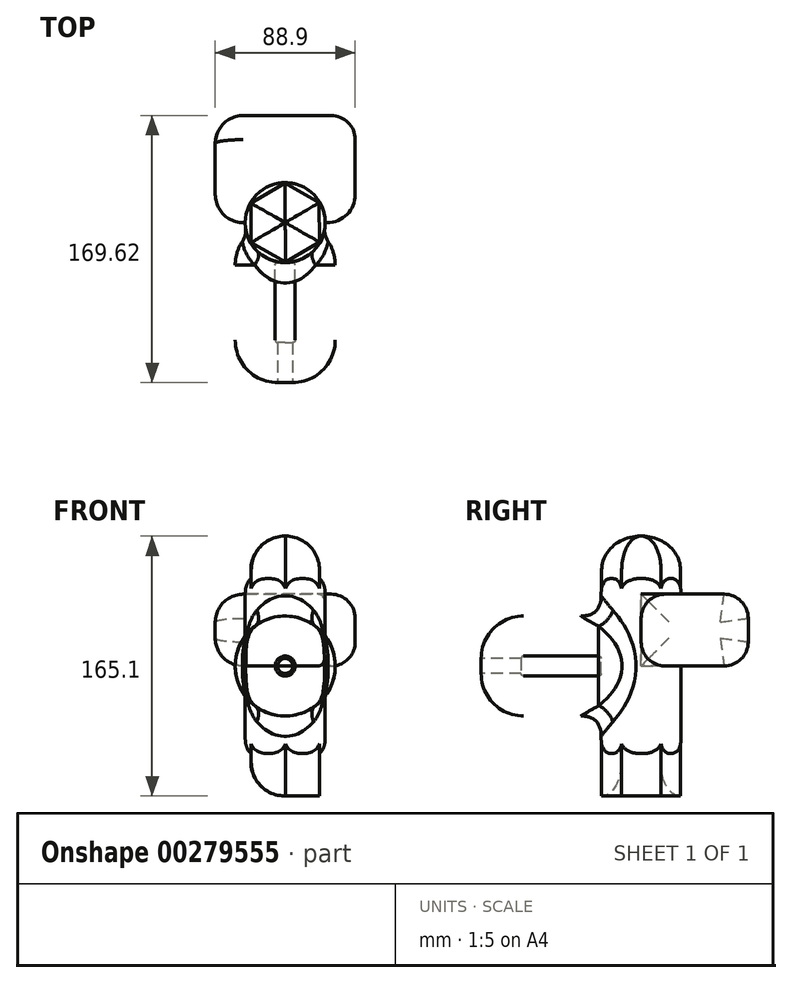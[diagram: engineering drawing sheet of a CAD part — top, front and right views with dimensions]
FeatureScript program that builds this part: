
annotation { "Feature Type Name" : "Feature", "Feature Type Description" : "" }
export const myFeature = defineFeature(function(context is Context, id is Id, definition is map)
    precondition{}
    {
        {
            var Q0;
            Q0=qCreatedBy(makeId("Front.planeOp"),FACE);
            var sketch = newSketch(context, id + "F0", { "sketchPlane" : qUnion([Q0])});
            skCircle(sketch, "E0", {"center": v(0, 0) * mm, "radius": 31.75 * mm});
            skSolve(sketch);
        }
        {
            var Q0;
            Q0=makeQuery(id+"F0.imprint","IMPRINT",FACE,{"disambiguationData":[TD([[makeQuery(id+"F0.imprint","IMPRINT",EDGE,{"derivedFrom":sQuery(id+"F0.wireOp",EDGE,"E0")}),1.0]])]});
            extrude(context, id + "F1", {"entities" : qUnion([Q0]), "depth" : 101.6 * mm});
        }
        {
            var Q0;
            Q0=makeQuery(id+"F1.opExtrude","CAP_FACE",FACE,{"disambiguationData":[OSD([sQuery(id+"F0.wireOp",EDGE,"E0")])],"isStart":false});
            var Q1;
            Q1=makeQuery(id+"F1.opExtrude","CAP_EDGE",EDGE,{"disambiguationData":[OSD([sQuery(id+"F0.wireOp",EDGE,"E0")])],"isStart":true});
            fillet(context, id + "F2", {"entities" : qUnion([Q0, Q1]), "radius" : 26.98 * mm, "tangentPropagation" : true, "allowEdgeOverflow" : false});
        }
        {
            var Q0;
            Q0=makeQuery(id+"F1.opExtrude","CAP_FACE",FACE,{"disambiguationData":[OSD([sQuery(id+"F0.wireOp",EDGE,"E0")])],"isStart":false});
            shell(context, id + "F3", {"entities" : qUnion([Q0]), "thickness" : 25.4 * mm});
        }
        {
            var Q0;
            Q0=qCreatedBy(makeId("Top.planeOp"),FACE);
            var sketch = newSketch(context, id + "F4", { "sketchPlane" : qUnion([Q0])});
            skCircle(sketch, "E1", {"center": v(0, 0) * mm, "radius": 25.4 * mm});
            skSolve(sketch);
        }
        {
            var Q0;
            Q0 = qSketchRegion(id + "F4", true);
            extrude(context, id + "F5", {"entities" : qUnion([Q0]), "operationType" : NewBodyOperationType.ADD, "endBound" : BoundingType.SYMMETRIC, "depth" : 116.84 * mm});
        }
        {
            var Q0;
            Q0=makeQuery(id+"F5.opExtrude","SWEPT_FACE",FACE,{"disambiguationData":[OSD([sQuery(id+"F4.wireOp",EDGE,"E1")])]});
            var Q1;
            Q1=makeQuery(id+"F5.opExtrude","CAP_EDGE",EDGE,{"disambiguationData":[OSD([sQuery(id+"F4.wireOp",EDGE,"E1")])],"isStart":false});
            fillet(context, id + "F6", {"entities" : qUnion([Q0, Q1]), "radius" : 12.88 * mm, "tangentPropagation" : true, "rho" : 0.5, "crossSection" : FilletCrossSection.CONIC, "allowEdgeOverflow" : false});
        }
        {
            var Q0;
            Q0=qCreatedBy(makeId("Right.planeOp"),FACE);
            var sketch = newSketch(context, id + "F7", { "sketchPlane" : qUnion([Q0])});
            skLineSegment(sketch, "E2.bottom", {"start": v(0, 0) * mm, "end": v(68.02, 0) * mm});
            skLineSegment(sketch, "E2.top", {"start": v(0, 45.65) * mm, "end": v(68.02, 45.65) * mm});
            skLineSegment(sketch, "E2.left", {"start": v(0, 0) * mm, "end": v(0, 45.65) * mm});
            skLineSegment(sketch, "E2.right", {"start": v(68.02, 0) * mm, "end": v(68.02, 45.65) * mm});
            skSolve(sketch);
        }
        {
            var Q0;
            Q0=makeQuery(id+"F7.imprint","IMPRINT",FACE,{"disambiguationData":[TD([[makeQuery(id+"F7.imprint","IMPRINT",EDGE,{"derivedFrom":sQuery(id+"F7.wireOp",EDGE,"E2.bottom")}),1.0]])]});
            extrude(context, id + "F8", {"entities" : qUnion([Q0]), "operationType" : NewBodyOperationType.ADD, "endBound" : BoundingType.SYMMETRIC, "depth" : 88.9 * mm});
        }
        {
            var Q0;
            Q0=makeQuery(id+"F8.opExtrude","CAP_FACE",FACE,{"disambiguationData":[OSD([sQuery(id+"F7.wireOp",EDGE,"E2.bottom"),sQuery(id+"F7.wireOp",EDGE,"E2.top"),sQuery(id+"F7.wireOp",EDGE,"E2.left"),sQuery(id+"F7.wireOp",EDGE,"E2.right")])],"isStart":true});
            var Q1;
            Q1=makeQuery(id+"F8.opExtrude","CAP_EDGE",EDGE,{"disambiguationData":[OSD([sQuery(id+"F7.wireOp",EDGE,"E2.left")])],"isStart":false});
            fillet(context, id + "F9", {"entities" : qUnion([Q0, Q1]), "radius" : 17.78 * mm, "tangentPropagation" : true, "allowEdgeOverflow" : false});
        }
        {
            var Q0;
            Q0=makeQuery(id+"F8.opExtrude","CAP_EDGE",EDGE,{"disambiguationData":[OSD([sQuery(id+"F7.wireOp",EDGE,"E2.right")])],"isStart":false});
            var Q1;
            Q1=makeQuery(id+"F9.opFillet","BLEND_FACE",FACE,{"disambiguationData":[OSD([sQuery(id+"F7.wireOp",EDGE,"E2.right")])]});
            var Q2;
            Q2=makeQuery(id+"F8.opExtrude","CAP_FACE",FACE,{"disambiguationData":[OSD([sQuery(id+"F7.wireOp",EDGE,"E2.bottom"),sQuery(id+"F7.wireOp",EDGE,"E2.top"),sQuery(id+"F7.wireOp",EDGE,"E2.left"),sQuery(id+"F7.wireOp",EDGE,"E2.right")])],"isStart":false});
            fillet(context, id + "F10", {"entities" : qUnion([Q0, Q1, Q2]), "radius" : 15.33 * mm, "tangentPropagation" : true, "allowEdgeOverflow" : false});
        }
        {
            var Q0;
            Q0=qCreatedBy(makeId("Top.planeOp"),FACE);
            var sketch = newSketch(context, id + "F11", { "sketchPlane" : qUnion([Q0])});
            skCircle(sketch, "E3.cCircle", {"center": v(0, 0) * mm, "radius": 21.7 * mm, "construction": true});
            skLineSegment(sketch, "E3.0", {"start": v(-0.19, 25.05) * mm, "end": v(21.6, 12.7) * mm});
            skLineSegment(sketch, "E3.1", {"start": v(21.6, 12.7) * mm, "end": v(21.8, -12.36) * mm});
            skLineSegment(sketch, "E3.2", {"start": v(21.8, -12.36) * mm, "end": v(0.19, -25.05) * mm});
            skLineSegment(sketch, "E3.3", {"start": v(0.19, -25.05) * mm, "end": v(-21.6, -12.7) * mm});
            skLineSegment(sketch, "E3.4", {"start": v(-21.6, -12.7) * mm, "end": v(-21.8, 12.36) * mm});
            skLineSegment(sketch, "E3.5", {"start": v(-21.8, 12.36) * mm, "end": v(-0.19, 25.05) * mm});
            skPoint(sketch, "E3.0.midPoint", {"position": v(10.7, 18.87) * mm});
            skSolve(sketch);
        }
        {
            var Q0;
            Q0 = qSketchRegion(id + "F11", true);
            extrude(context, id + "F12", {"entities" : qUnion([Q0]), "operationType" : NewBodyOperationType.ADD, "endBound" : BoundingType.SYMMETRIC, "depth" : 165.1 * mm});
        }
        {
            var Q0;
            Q0=makeQuery(id+"F12.opExtrude","CAP_EDGE",EDGE,{"disambiguationData":[OSD([sQuery(id+"F11.wireOp",EDGE,"E3.4")])],"isStart":true});
            var Q1;
            Q1=makeQuery(id+"F12.opExtrude","CAP_FACE",FACE,{"disambiguationData":[OSD([sQuery(id+"F11.wireOp",EDGE,"E3.0"),sQuery(id+"F11.wireOp",EDGE,"E3.1"),sQuery(id+"F11.wireOp",EDGE,"E3.2"),sQuery(id+"F11.wireOp",EDGE,"E3.3"),sQuery(id+"F11.wireOp",EDGE,"E3.4"),sQuery(id+"F11.wireOp",EDGE,"E3.5")])],"isStart":false});
            fillet(context, id + "F13", {"entities" : qUnion([Q0, Q1]), "radius" : 21.46 * mm, "tangentPropagation" : true, "allowEdgeOverflow" : false});
        }
    });
